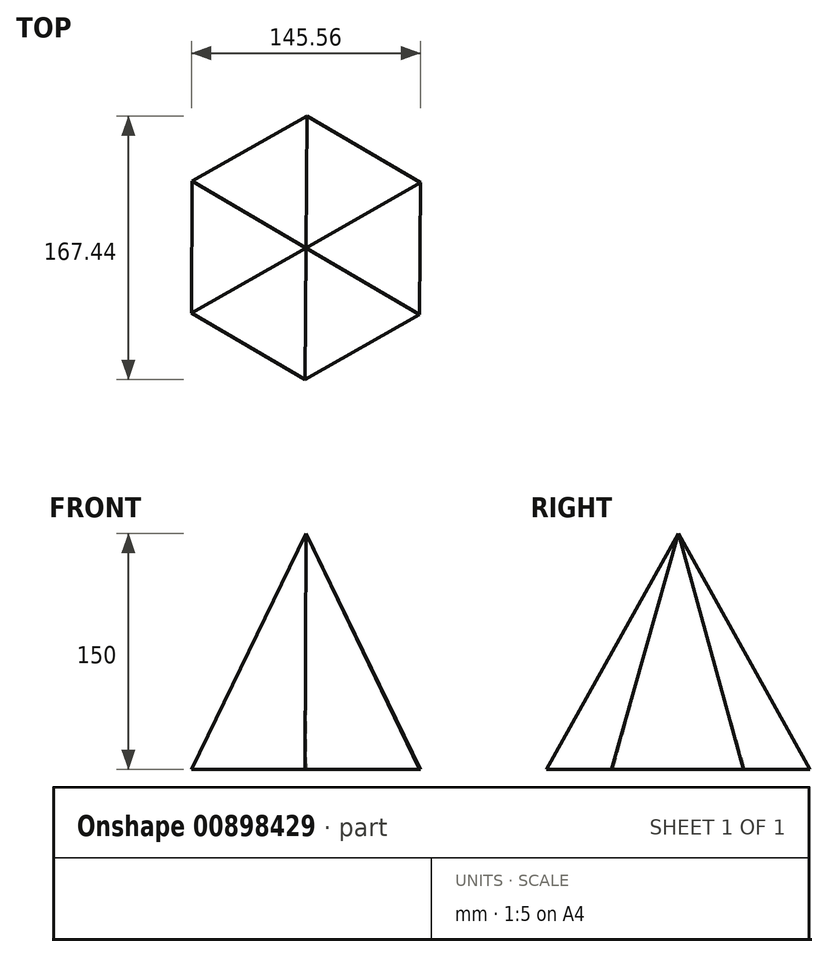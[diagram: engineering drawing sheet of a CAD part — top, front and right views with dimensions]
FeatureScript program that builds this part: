
annotation { "Feature Type Name" : "Feature", "Feature Type Description" : "" }
export const myFeature = defineFeature(function(context is Context, id is Id, definition is map)
    precondition{}
    {
        {
            var Q0;
            Q0=qCreatedBy(makeId("Top.planeOp"),FACE);
            var sketch = newSketch(context, id + "F0", { "sketchPlane" : qUnion([Q0])});
            skCircle(sketch, "E0.cCircle", {"center": v(0, 0) * mm, "radius": 72.5 * mm, "construction": true});
            skLineSegment(sketch, "E0.0", {"start": v(72.22, -42.34) * mm, "end": v(-0.56, -83.72) * mm});
            skLineSegment(sketch, "E0.1", {"start": v(-0.56, -83.72) * mm, "end": v(-72.78, -41.38) * mm});
            skLineSegment(sketch, "E0.2", {"start": v(-72.78, -41.38) * mm, "end": v(-72.22, 42.34) * mm});
            skLineSegment(sketch, "E0.3", {"start": v(-72.22, 42.34) * mm, "end": v(0.56, 83.72) * mm});
            skLineSegment(sketch, "E0.4", {"start": v(0.56, 83.72) * mm, "end": v(72.78, 41.38) * mm});
            skLineSegment(sketch, "E0.5", {"start": v(72.78, 41.38) * mm, "end": v(72.22, -42.34) * mm});
            skPoint(sketch, "E0.0.midPoint", {"position": v(35.83, -63.03) * mm});
            skSolve(sketch);
        }
        {
            var Q0;
            Q0=qCreatedBy(makeId("Top.planeOp"),FACE);
            cPlane(context, id + "F1", {"entities" : qUnion([Q0]), "cplaneType" : CPlaneType.OFFSET, "offset" : 150 * mm, "width" : 150 * mm, "height" : 150 * mm});
        }
        {
            var Q0;
            Q0=qCreatedBy(id+"F1.planeOp",FACE);
            var sketch = newSketch(context, id + "F2", { "sketchPlane" : qUnion([Q0])});
            skPoint(sketch, "E1", {"position": v(0, 0) * mm});
            skSolve(sketch);
        }
        {
            var Q0;
            Q0=makeQuery(id+"F0.imprint","IMPRINT",FACE,{"disambiguationData":[TD([[makeQuery(id+"F0.imprint","IMPRINT",EDGE,{"derivedFrom":sQuery(id+"F0.wireOp",EDGE,"E0.0")}),-1.0]])]});
            var Q1;
            Q1=sQuery(id+"F2.wireOp",VERTEX,"E1");
            loft(context, id + "F3", {"sheetProfilesArray" : [{ "sheetProfileEntities" : qUnion([Q0]) }, { "sheetProfileEntities" : qUnion([Q1]) }]});
        }
    });
